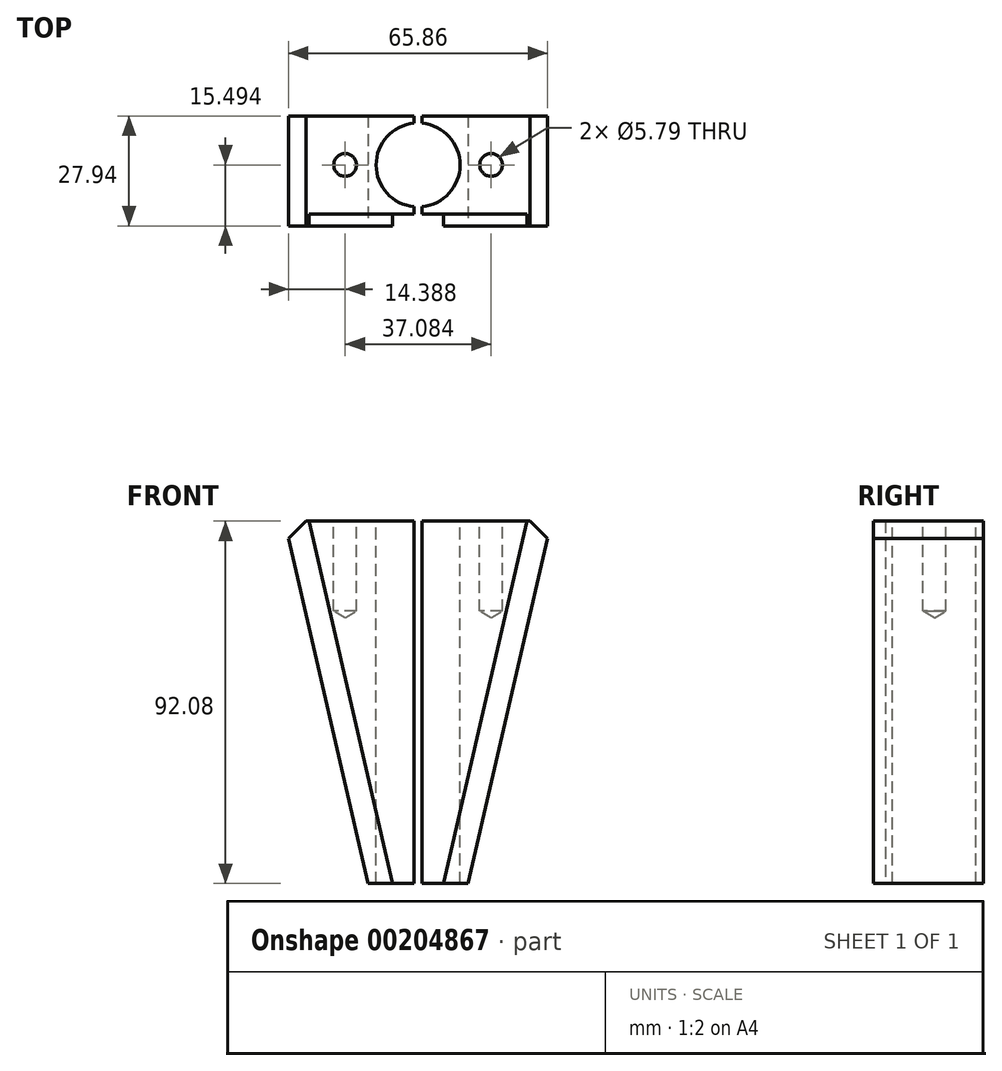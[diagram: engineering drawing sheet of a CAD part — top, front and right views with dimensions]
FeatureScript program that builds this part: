
annotation { "Feature Type Name" : "Feature", "Feature Type Description" : "" }
export const myFeature = defineFeature(function(context is Context, id is Id, definition is map)
    precondition{}
    {
        {
            var Q0;
            Q0=qCreatedBy(makeId("Front.planeOp"),FACE);
            var sketch = newSketch(context, id + "F0", { "sketchPlane" : qUnion([Q0])});
            skLineSegment(sketch, "E0", {"start": v(32.93, -4.44) * mm, "end": v(12.7, -92.08) * mm});
            skLineSegment(sketch, "E1", {"start": v(12.7, -92.08) * mm, "end": v(-12.7, -92.08) * mm});
            skLineSegment(sketch, "E2", {"start": v(-12.7, -92.08) * mm, "end": v(-32.93, -4.44) * mm});
            skLineSegment(sketch, "E3", {"start": v(0, 0) * mm, "end": v(0, -92.08) * mm, "construction": true});
            skLineSegment(sketch, "E4", {"start": v(-28.49, 0) * mm, "end": v(28.49, 0) * mm});
            skLineSegment(sketch, "E5", {"start": v(28.49, 0) * mm, "end": v(32.93, -4.44) * mm});
            skLineSegment(sketch, "E6", {"start": v(-28.49, 0) * mm, "end": v(-32.93, -4.45) * mm});
            skSolve(sketch);
        }
        {
            var Q0;
            Q0=makeQuery(id+"F0.imprint","IMPRINT",FACE,{"disambiguationData":[TD([[makeQuery(id+"F0.imprint","IMPRINT",EDGE,{"derivedFrom":sQuery(id+"F0.wireOp",EDGE,"4KXuys1P-PTsJ-30CA-ikOH-Se8BkncmhGfz")}),-1.0]])]});
            var Q1;
            Q1=makeQuery(id+"F0.imprint","IMPRINT",FACE,{"disambiguationData":[TD([[makeQuery(id+"F0.imprint","IMPRINT",EDGE,{"derivedFrom":sQuery(id+"F0.wireOp",EDGE,"E0")}),-1.0]])]});
            extrude(context, id + "F1", {"entities" : qUnion([Q0, Q1]), "oppositeDirection" : true, "depth" : 27.94 * mm});
        }
        {
            var Q0;
            Q0=makeQuery(id+"F1.opExtrude","CAP_FACE",FACE,{"disambiguationData":[OSD([sQuery(id+"F0.wireOp",EDGE,"4KXuys1P-PTsJ-30CA-ikOH-Se8BkncmhGfz"),sQuery(id+"F0.wireOp",EDGE,"a1VgrxVP-YlZw-Qevx-WVVU-paKObhud19An"),sQuery(id+"F0.wireOp",EDGE,"E0"),sQuery(id+"F0.wireOp",EDGE,"E1"),sQuery(id+"F0.wireOp",EDGE,"E2"),sQuery(id+"F0.wireOp",EDGE,"cIpZIlDj-Ag8D-xa2x-RwRU-nTf3DJYwZ5lU")])],"isStart":true});
            var sketch = newSketch(context, id + "F2", { "sketchPlane" : qUnion([Q0])});
            skLineSegment(sketch, "E7", {"start": v(-6.44, -92.08) * mm, "end": v(-27.7, 0) * mm});
            skLineSegment(sketch, "E8", {"start": v(6.44, -92.08) * mm, "end": v(27.7, 0) * mm});
            skLineSegment(sketch, "E9", {"start": v(27.7, 0) * mm, "end": v(-27.7, 0) * mm});
            skLineSegment(sketch, "E10", {"start": v(-6.44, -92.08) * mm, "end": v(6.44, -92.07) * mm});
            skSolve(sketch);
        }
        {
            var Q0;
            Q0=makeQuery(id+"F2.imprint","IMPRINT",FACE,{"disambiguationData":[TD([[makeQuery(id+"F2.imprint","IMPRINT",EDGE,{"derivedFrom":sQuery(id+"F2.wireOp",EDGE,"E7")}),-1.0]])]});
            extrude(context, id + "F3", {"entities" : qUnion([Q0]), "operationType" : NewBodyOperationType.REMOVE, "oppositeDirection" : true, "depth" : 3.05 * mm});
        }
        {
            var Q0;
            Q0=makeQuery(id+"F1.opExtrude","SWEPT_FACE",FACE,{"disambiguationData":[OSD([sQuery(id+"F0.wireOp",EDGE,"E4")])]});
            var sketch = newSketch(context, id + "F4", { "sketchPlane" : qUnion([Q0])});
            skCircle(sketch, "E11", {"center": v(-18.54, 15.5) * mm, "radius": 2.7 * mm});
            skCircle(sketch, "E12", {"center": v(18.54, 15.5) * mm, "radius": 2.7 * mm});
            skSolve(sketch);
        }
        {
            var Q0;
            Q0=sQuery(id+"F4.wireOp",VERTEX,"E11.center");
            var Q1;
            Q1=sQuery(id+"F4.wireOp",VERTEX,"E12.center");
            var Q2;
            Q2=makeQuery(id+"F1.opExtrude","SWEPT_BODY",BODY,{"disambiguationData":[OSD([sQuery(id+"F0.wireOp",EDGE,"E0"),sQuery(id+"F0.wireOp",EDGE,"E1"),sQuery(id+"F0.wireOp",EDGE,"E2"),sQuery(id+"F0.wireOp",EDGE,"E4"),sQuery(id+"F0.wireOp",EDGE,"E5"),sQuery(id+"F0.wireOp",EDGE,"E6")])]});
            hole(context, id + "F5", {"style" : HoleStyle.SIMPLE, "endStyle" : HoleEndStyle.BLIND, "standardTappedOrClearance" : lookupTablePath({ "standard" : "ANSI", "engagement" : "50%", "pitch" : "28 tpi", "size" : "1/4", "type" : "Tapped" }), "standardBlindInLast" : lookupTablePath({ "standard" : "ANSI", "engagement" : "50%", "pitch" : "28 tpi", "size" : "1/4", "type" : "Tapped" }), "holeDiameter" : 5.8 * mm, "holeDepth" : 22.86 * mm, "locations" : qUnion([Q0, Q1]), "scope" : qUnion([Q2]), "majorDiameter" : 6.35 * mm});
        }
        {
            var Q0;
            Q0=makeQuery(id+"F1.opExtrude","SWEPT_FACE",FACE,{"disambiguationData":[OSD([sQuery(id+"F0.wireOp",EDGE,"E4")])]});
            var sketch = newSketch(context, id + "F6", { "sketchPlane" : qUnion([Q0])});
            skCircle(sketch, "E13", {"center": v(0, 15.5) * mm, "radius": 9.13 * mm});
            skSolve(sketch);
        }
        {
            var Q0;
            Q0=sQuery(id+"F6.wireOp",VERTEX,"E13.center");
            var Q1;
            Q1=makeQuery(id+"F1.opExtrude","SWEPT_BODY",BODY,{"disambiguationData":[OSD([sQuery(id+"F0.wireOp",EDGE,"E0"),sQuery(id+"F0.wireOp",EDGE,"E1"),sQuery(id+"F0.wireOp",EDGE,"E2"),sQuery(id+"F0.wireOp",EDGE,"E4"),sQuery(id+"F0.wireOp",EDGE,"E5"),sQuery(id+"F0.wireOp",EDGE,"E6")])]});
            hole(context, id + "F7", {"style" : HoleStyle.SIMPLE, "endStyle" : HoleEndStyle.THROUGH, "holeDiameter" : 21.34 * mm, "locations" : qUnion([Q0]), "scope" : qUnion([Q1]), "tappedDepth" : 12.7 * mm, "tapClearance" : 3});
        }
        {
            var Q0;
            Q0=makeQuery(id+"F3.boolean.opBoolean","COPY",FACE,{"derivedFrom":makeQuery(id+"F3.opExtrude","CAP_FACE",FACE,{"disambiguationData":[OSD([sQuery(id+"F2.wireOp",EDGE,"E7"),sQuery(id+"F2.wireOp",EDGE,"E8"),sQuery(id+"F2.wireOp",EDGE,"E9"),sQuery(id+"F2.wireOp",EDGE,"E10")])],"isStart":false})});
            var sketch = newSketch(context, id + "F8", { "sketchPlane" : qUnion([Q0])});
            skLineSegment(sketch, "E14.bottom", {"start": v(-1.02, 0) * mm, "end": v(1.02, 0) * mm});
            skLineSegment(sketch, "E14.top", {"start": v(-1.02, -92.08) * mm, "end": v(1.02, -92.08) * mm});
            skLineSegment(sketch, "E14.left", {"start": v(-1.02, 0) * mm, "end": v(-1.02, -92.08) * mm});
            skLineSegment(sketch, "E14.right", {"start": v(1.02, 0) * mm, "end": v(1.02, -92.08) * mm});
            skSolve(sketch);
        }
        {
            var Q0;
            Q0=makeQuery(id+"F8.imprint","IMPRINT",FACE,{"disambiguationData":[TD([[makeQuery(id+"F8.imprint","IMPRINT",EDGE,{"derivedFrom":sQuery(id+"F8.wireOp",EDGE,"E14.bottom")}),-1.0]])]});
            extrude(context, id + "F9", {"entities" : qUnion([Q0]), "operationType" : NewBodyOperationType.REMOVE, "endBound" : BoundingType.THROUGH_ALL, "oppositeDirection" : true, "depth" : 25.4 * mm});
        }
    });
